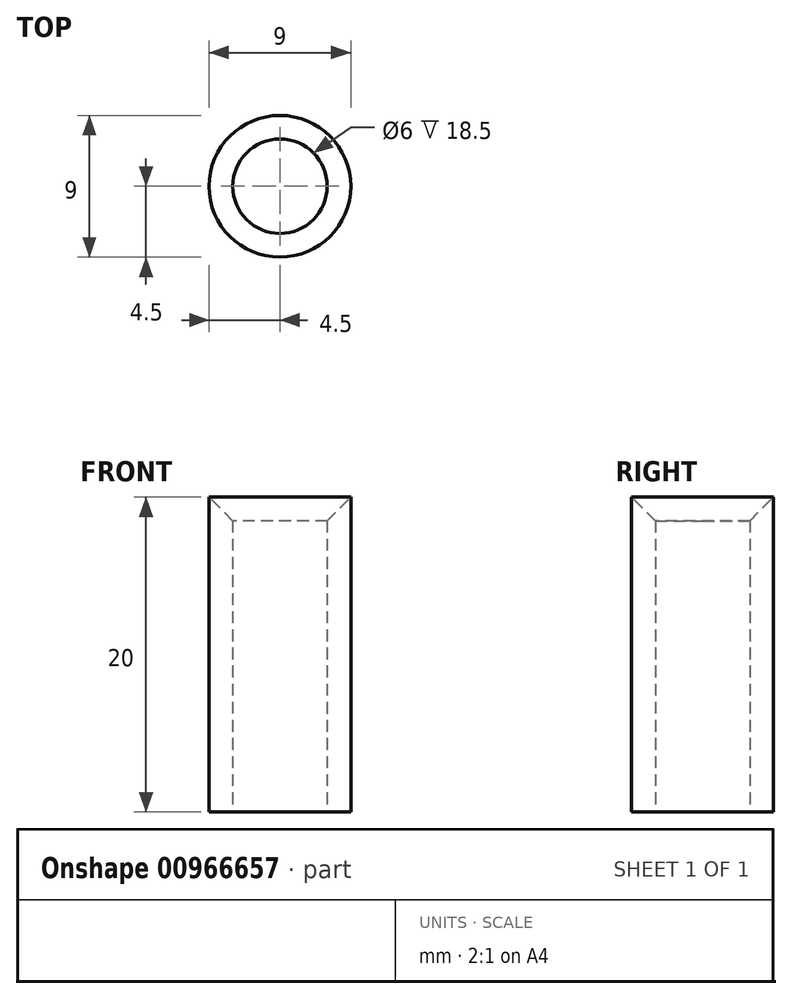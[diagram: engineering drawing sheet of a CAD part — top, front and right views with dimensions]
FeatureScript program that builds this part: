
annotation { "Feature Type Name" : "Feature", "Feature Type Description" : "" }
export const myFeature = defineFeature(function(context is Context, id is Id, definition is map)
    precondition{}
    {
        {
            var Q0;
            Q0=qCreatedBy(makeId("Top.planeOp"),FACE);
            var sketch = newSketch(context, id + "F0", { "sketchPlane" : qUnion([Q0])});
            skCircle(sketch, "E0", {"center": v(0, 0) * mm, "radius": 4.5 * mm});
            skCircle(sketch, "E1", {"center": v(0, 0) * mm, "radius": 3 * mm});
            skSolve(sketch);
        }
        {
            var Q0;
            Q0 = qSketchRegion(id + "F0", true);
            extrude(context, id + "F1", {"entities" : qUnion([Q0]), "depth" : 20 * mm, "offsetDistance" : 25 * mm});
        }
        {
            var Q0;
            Q0=makeQuery(id+"F1.opExtrude","CAP_FACE",FACE,{"disambiguationData":[OSD([sQuery(id+"F0.wireOp",EDGE,"E0"),sQuery(id+"F0.wireOp",EDGE,"E1")])],"isStart":false});
            var sketch = newSketch(context, id + "F2", { "sketchPlane" : qUnion([Q0])});
            skPoint(sketch, "E2", {"position": v(0, 0) * mm});
            skPoint(sketch, "E3", {"position": v(4.5, 0) * mm});
            skLineSegment(sketch, "E4", {"start": v(0, 0) * mm, "end": v(0, 4.5) * mm});
            skLineSegment(sketch, "E5", {"start": v(0, 4.5) * mm, "end": v(-4.5, 0) * mm});
            skLineSegment(sketch, "E6", {"start": v(-4.5, 0) * mm, "end": v(0, -4.5) * mm});
            skLineSegment(sketch, "E7", {"start": v(0, -4.5) * mm, "end": v(4.5, 0) * mm});
            skLineSegment(sketch, "E8", {"start": v(0, 4.5) * mm, "end": v(4.5, 0) * mm});
            skLineSegment(sketch, "E9", {"start": v(0, 0) * mm, "end": v(-4.5, 0) * mm});
            skLineSegment(sketch, "E10", {"start": v(0, 0) * mm, "end": v(0, -4.5) * mm});
            skLineSegment(sketch, "E11", {"start": v(4.5, 0) * mm, "end": v(0, 0) * mm});
            skSolve(sketch);
        }
        {
            var Q0;
            Q0=sQuery(id+"F2.wireOp",VERTEX,"E2");
            var Q1;
            Q1=makeQuery(id+"F1.opExtrude","SWEPT_BODY",BODY,{"disambiguationData":[OSD([sQuery(id+"F0.wireOp",EDGE,"E0"),sQuery(id+"F0.wireOp",EDGE,"E1")])]});
            hole(context, id + "F3", {"style" : HoleStyle.C_SINK, "endStyle" : HoleEndStyle.THROUGH, "holeDiameter" : 6 * mm, "cSinkDiameter" : 9 * mm, "cSinkAngle" : 90 * degree, "majorDiameter" : 5 * mm, "isTappedThrough" : true, "tappedDepth" : 12 * mm, "tapClearance" : 3, "locations" : qUnion([Q0]), "scope" : qUnion([Q1])});
        }
    });
